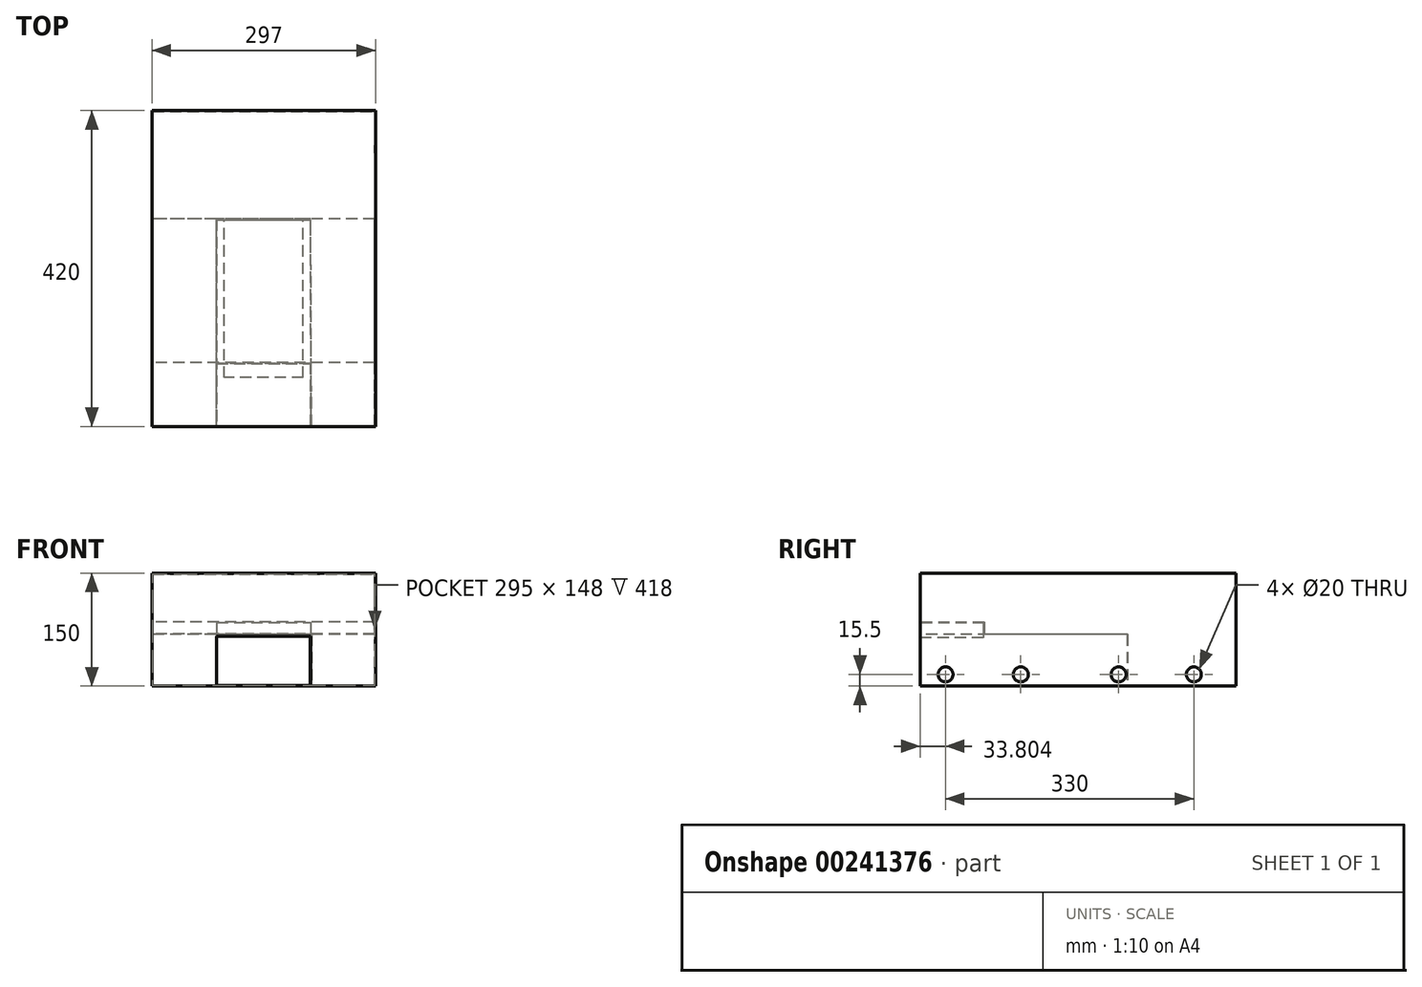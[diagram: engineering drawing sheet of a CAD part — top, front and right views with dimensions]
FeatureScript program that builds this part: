
annotation { "Feature Type Name" : "Feature", "Feature Type Description" : "" }
export const myFeature = defineFeature(function(context is Context, id is Id, definition is map)
    precondition{}
    {
        {
            var Q0;
            Q0=qCreatedBy(makeId("Top.planeOp"),FACE);
            var sketch = newSketch(context, id + "F0", { "sketchPlane" : qUnion([Q0])});
            skLineSegment(sketch, "E0.bottom", {"start": v(-148.5, 210) * mm, "end": v(148.5, 210) * mm});
            skLineSegment(sketch, "E0.top", {"start": v(-148.5, -210) * mm, "end": v(148.5, -210) * mm});
            skLineSegment(sketch, "E0.left", {"start": v(-148.5, 210) * mm, "end": v(-148.5, -210) * mm});
            skLineSegment(sketch, "E0.right", {"start": v(148.5, 210) * mm, "end": v(148.5, -210) * mm});
            skPoint(sketch, "E0.middle", {"position": v(0, 0) * mm});
            skSolve(sketch);
        }
        {
            var Q0;
            Q0 = qSketchRegion(id + "F0", true);
            extrude(context, id + "F1", {"entities" : qUnion([Q0]), "depth" : 150 * mm});
        }
        {
            var Q0;
            Q0=makeQuery(id+"F1.opExtrude","CAP_FACE",FACE,{"disambiguationData":[OSD([sQuery(id+"F0.wireOp",EDGE,"E0.bottom"),sQuery(id+"F0.wireOp",EDGE,"E0.top"),sQuery(id+"F0.wireOp",EDGE,"E0.left"),sQuery(id+"F0.wireOp",EDGE,"E0.right")])],"isStart":false});
            var sketch = newSketch(context, id + "F2", { "sketchPlane" : qUnion([Q0])});
            skLineSegment(sketch, "E1.bottom", {"start": v(-147.5, 209) * mm, "end": v(147.5, 209) * mm});
            skLineSegment(sketch, "E1.top", {"start": v(-147.5, -209) * mm, "end": v(147.5, -209) * mm});
            skLineSegment(sketch, "E1.left", {"start": v(-147.5, 209) * mm, "end": v(-147.5, -209) * mm});
            skLineSegment(sketch, "E1.right", {"start": v(147.5, 209) * mm, "end": v(147.5, -209) * mm});
            skPoint(sketch, "E1.middle", {"position": v(0, 0) * mm});
            skSolve(sketch);
        }
        {
            var Q0;
            Q0 = qSketchRegion(id + "F2", true);
            extrude(context, id + "F3", {"entities" : qUnion([Q0]), "operationType" : NewBodyOperationType.REMOVE, "oppositeDirection" : true, "depth" : 149 * mm, "hasSecondDirection" : true, "secondDirectionOppositeDirection" : false, "secondDirectionDepth" : -1 * mm});
        }
        {
            var Q0;
            Q0=makeQuery(id+"F1.opExtrude","SWEPT_FACE",FACE,{"disambiguationData":[OSD([sQuery(id+"F0.wireOp",EDGE,"E0.top")])]});
            var sketch = newSketch(context, id + "F4", { "sketchPlane" : qUnion([Q0])});
            skLineSegment(sketch, "E2.bottom", {"start": v(-62.5, 1) * mm, "end": v(62.5, 1) * mm});
            skLineSegment(sketch, "E2.top", {"start": v(-62.5, 66) * mm, "end": v(62.5, 66) * mm});
            skLineSegment(sketch, "E2.left", {"start": v(-62.5, 1) * mm, "end": v(-62.5, 66) * mm});
            skLineSegment(sketch, "E2.right", {"start": v(62.5, 1) * mm, "end": v(62.5, 66) * mm});
            skSolve(sketch);
        }
        {
            var Q0;
            Q0 = qSketchRegion(id + "F4", true);
            extrude(context, id + "F5", {"entities" : qUnion([Q0]), "operationType" : NewBodyOperationType.REMOVE, "oppositeDirection" : true, "depth" : 25 * mm});
        }
        {
            var Q0;
            Q0=qCreatedBy(makeId("Top.planeOp"),FACE);
            var sketch = newSketch(context, id + "F6", { "sketchPlane" : qUnion([Q0])});
            skLineSegment(sketch, "E3.bottom", {"start": v(-52.5, 65) * mm, "end": v(52.5, 65) * mm});
            skLineSegment(sketch, "E3.top", {"start": v(-52.5, -145) * mm, "end": v(52.5, -145) * mm});
            skLineSegment(sketch, "E3.left", {"start": v(-52.5, 65) * mm, "end": v(-52.5, -145) * mm});
            skLineSegment(sketch, "E3.right", {"start": v(52.5, 65) * mm, "end": v(52.5, -145) * mm});
            skSolve(sketch);
        }
        {
            var Q0;
            Q0 = qSketchRegion(id + "F6", true);
            extrude(context, id + "F7", {"entities" : qUnion([Q0]), "operationType" : NewBodyOperationType.REMOVE, "depth" : 25 * mm});
        }
        {
            var Q0;
            Q0=makeQuery(id+"F5.boolean.opBoolean","MERGE",FACE,{"derivedFrom":[makeQuery(id+"F3.boolean.opBoolean","COPY",FACE,{"derivedFrom":makeQuery(id+"F3.opExtrude","CAP_FACE",FACE,{"disambiguationData":[OSD([sQuery(id+"F2.wireOp",EDGE,"E1.bottom"),sQuery(id+"F2.wireOp",EDGE,"E1.top"),sQuery(id+"F2.wireOp",EDGE,"E1.left"),sQuery(id+"F2.wireOp",EDGE,"E1.right")])],"isStart":false})}),makeQuery(id+"F5.opExtrude","SWEPT_FACE",FACE,{"disambiguationData":[OSD([sQuery(id+"F4.wireOp",EDGE,"E2.bottom")])]})]});
            var sketch = newSketch(context, id + "F8", { "sketchPlane" : qUnion([Q0])});
            skLineSegment(sketch, "E4", {"start": v(-62.5, -209) * mm, "end": v(-62.5, 65) * mm});
            skLineSegment(sketch, "E5", {"start": v(-62.5, 65) * mm, "end": v(61.5, 65) * mm});
            skLineSegment(sketch, "E6", {"start": v(61.5, 65) * mm, "end": v(62.5, -209) * mm});
            skLineSegment(sketch, "E7", {"start": v(62.5, -209) * mm, "end": v(63.5, -209) * mm});
            skLineSegment(sketch, "E8", {"start": v(63.5, -209) * mm, "end": v(62.5, 66) * mm});
            skLineSegment(sketch, "E9", {"start": v(62.5, 66) * mm, "end": v(-63.5, 66) * mm});
            skLineSegment(sketch, "E10", {"start": v(-63.5, 66) * mm, "end": v(-63.5, -209) * mm});
            skLineSegment(sketch, "E11", {"start": v(-63.5, -209) * mm, "end": v(-62.5, -209) * mm});
            skSolve(sketch);
        }
        {
            var Q0;
            Q0 = qSketchRegion(id + "F8", true);
            extrude(context, id + "F9", {"entities" : qUnion([Q0]), "operationType" : NewBodyOperationType.ADD, "depth" : 67.5 * mm});
        }
        {
            var Q0;
            Q0=makeQuery(id+"F3.boolean.opBoolean","COPY",FACE,{"derivedFrom":makeQuery(id+"F3.opExtrude","SWEPT_FACE",FACE,{"disambiguationData":[OSD([sQuery(id+"F2.wireOp",EDGE,"E1.left")])]})});
            var sketch = newSketch(context, id + "F10", { "sketchPlane" : qUnion([Q0])});
            skLineSegment(sketch, "E12", {"start": v(66, 68.5) * mm, "end": v(66, 69.5) * mm});
            skLineSegment(sketch, "E13", {"start": v(66, 69.5) * mm, "end": v(-125, 69.5) * mm});
            skLineSegment(sketch, "E14", {"start": v(-125, 69.5) * mm, "end": v(-125, 85.5) * mm});
            skLineSegment(sketch, "E15", {"start": v(-125, 85.5) * mm, "end": v(-209, 85.5) * mm});
            skLineSegment(sketch, "E16", {"start": v(66, 68.5) * mm, "end": v(-126, 68.5) * mm});
            skLineSegment(sketch, "E17", {"start": v(-126, 68.5) * mm, "end": v(-126, 84.5) * mm});
            skLineSegment(sketch, "E18", {"start": v(-126, 84.5) * mm, "end": v(-209.08, 84.5) * mm});
            skLineSegment(sketch, "E19", {"start": v(-209.08, 84.5) * mm, "end": v(-209, 85.5) * mm});
            skSolve(sketch);
        }
        {
            var Q0;
            Q0 = qSketchRegion(id + "F10", true);
            extrude(context, id + "F11", {"entities" : qUnion([Q0]), "operationType" : NewBodyOperationType.ADD, "endBound" : BoundingType.UP_TO_NEXT, "depth" : 25 * mm});
        }
        {
            var Q0;
            Q0=qCreatedBy(makeId("Right.planeOp"),FACE);
            var sketch = newSketch(context, id + "F12", { "sketchPlane" : qUnion([Q0])});
            skLineSegment(sketch, "E20", {"start": v(-126, 68.5) * mm, "end": v(-209, 68.5) * mm});
            skLineSegment(sketch, "E21", {"start": v(-209, 68.5) * mm, "end": v(-209, 69.5) * mm});
            skLineSegment(sketch, "E22", {"start": v(-209, 69.5) * mm, "end": v(-126, 69.5) * mm});
            skLineSegment(sketch, "E23", {"start": v(-126, 69.5) * mm, "end": v(-126, 68.5) * mm});
            skSolve(sketch);
        }
        {
            var Q0;
            Q0 = qSketchRegion(id + "F12", true);
            extrude(context, id + "F13", {"entities" : qUnion([Q0]), "operationType" : NewBodyOperationType.ADD, "endBound" : BoundingType.SYMMETRIC, "depth" : 297 * mm});
        }
        {
            var Q0;
            Q0=qCreatedBy(makeId("Right.planeOp"),FACE);
            var sketch = newSketch(context, id + "F14", { "sketchPlane" : qUnion([Q0])});
            skLineSegment(sketch, "E24", {"start": v(-126, 84.5) * mm, "end": v(-126, 64.5) * mm});
            skLineSegment(sketch, "E25", {"start": v(-126, 64.5) * mm, "end": v(-209, 64.5) * mm});
            skLineSegment(sketch, "E26", {"start": v(-209, 64.5) * mm, "end": v(-209, 84.5) * mm});
            skLineSegment(sketch, "E27", {"start": v(-209, 84.5) * mm, "end": v(-126, 84.5) * mm});
            skSolve(sketch);
        }
        {
            var Q0;
            Q0=makeQuery(id+"F13.boolean.opBoolean","SPLIT",FACE,{"disambiguationData":[TD([makeQuery(id+"F11.opExtrude","SWEPT_FACE",FACE,{"disambiguationData":[OSD([sQuery(id+"F10.wireOp",EDGE,"E17")])]})])],"derivedFrom":makeQuery(id+"F3.boolean.opBoolean","COPY",FACE,{"derivedFrom":makeQuery(id+"F3.opExtrude","SWEPT_FACE",FACE,{"disambiguationData":[OSD([sQuery(id+"F2.wireOp",EDGE,"E1.left")])]})})});
            var sketch = newSketch(context, id + "F15", { "sketchPlane" : qUnion([Q0])});
            skLineSegment(sketch, "E28.bottom", {"start": v(-209, 84.5) * mm, "end": v(-126, 84.5) * mm});
            skLineSegment(sketch, "E28.top", {"start": v(-209, 69.5) * mm, "end": v(-126, 69.5) * mm});
            skLineSegment(sketch, "E28.left", {"start": v(-209, 84.5) * mm, "end": v(-209, 69.5) * mm});
            skLineSegment(sketch, "E28.right", {"start": v(-126, 84.5) * mm, "end": v(-126, 69.5) * mm});
            skSolve(sketch);
        }
        {
            var Q0;
            Q0 = qSketchRegion(id + "F15", true);
            extrude(context, id + "F16", {"entities" : qUnion([Q0]), "operationType" : NewBodyOperationType.ADD, "endBound" : BoundingType.UP_TO_NEXT, "depth" : 25 * mm});
        }
        {
            var Q0;
            Q0 = qSketchRegion(id + "F14", true);
            extrude(context, id + "F17", {"entities" : qUnion([Q0]), "operationType" : NewBodyOperationType.REMOVE, "endBound" : BoundingType.SYMMETRIC, "oppositeDirection" : true, "depth" : 125 * mm});
        }
        {
            var Q0;
            Q0=makeQuery(id+"F1.opExtrude","SWEPT_FACE",FACE,{"disambiguationData":[OSD([sQuery(id+"F0.wireOp",EDGE,"E0.right")])]});
            var sketch = newSketch(context, id + "F18", { "sketchPlane" : qUnion([Q0])});
            skCircle(sketch, "E29", {"center": v(-176.2, 15.5) * mm, "radius": 10 * mm});
            skCircle(sketch, "E30", {"center": v(-76.2, 15.5) * mm, "radius": 10 * mm});
            skCircle(sketch, "E31", {"center": v(53.8, 15.5) * mm, "radius": 10 * mm});
            skCircle(sketch, "E32", {"center": v(153.8, 15.5) * mm, "radius": 10 * mm});
            skSolve(sketch);
        }
        {
            var Q0;
            Q0=makeQuery(id+"F18.imprint","IMPRINT",FACE,{"disambiguationData":[TD([[makeQuery(id+"F18.imprint","IMPRINT",EDGE,{"derivedFrom":sQuery(id+"F18.wireOp",EDGE,"E29")}),1.0]])]});
            var Q1;
            Q1=makeQuery(id+"F18.imprint","IMPRINT",FACE,{"disambiguationData":[TD([[makeQuery(id+"F18.imprint","IMPRINT",EDGE,{"derivedFrom":sQuery(id+"F18.wireOp",EDGE,"E30")}),1.0]])]});
            var Q2;
            Q2=makeQuery(id+"F18.imprint","IMPRINT",FACE,{"disambiguationData":[TD([[makeQuery(id+"F18.imprint","IMPRINT",EDGE,{"derivedFrom":sQuery(id+"F18.wireOp",EDGE,"E31")}),1.0]])]});
            var Q3;
            Q3=makeQuery(id+"F18.imprint","IMPRINT",FACE,{"disambiguationData":[TD([[makeQuery(id+"F18.imprint","IMPRINT",EDGE,{"derivedFrom":sQuery(id+"F18.wireOp",EDGE,"E32")}),1.0]])]});
            extrude(context, id + "F19", {"entities" : qUnion([Q0, Q1, Q2, Q3]), "operationType" : NewBodyOperationType.REMOVE, "oppositeDirection" : true, "depth" : 7.5 * mm});
        }
    });
